# Revit family: TSM Betonschraube Ansatzschraube TSM 6, vz M 8x 16
name_source: partatom
category: Allgemeines Modell
revit_build: Autodesk Revit 2017 (Build: 20190507_1515(x64)
units: mm (PartAtom-declared; Revit-internal decimal feet)

## family parameters
Arbeitsebenenbasiert = Ja
Beim Laden mit Abzugskörper schneiden = Nein
Bemaßung runder Anschluss = Durchmesser verwenden
Gemeinsam genutzt = Ja
Immer vertikal = Nein
Kann Basisbauteil für Bewehrung sein = Nein
Raumberechnungspunkt = Nein
Teiletyp = Normal

## types (1)
- TSM Betonschraube Ansatzschraube TSM 6, vz M 8x 16
    Artikelnummer = 2230002
    Außengewinde = M8 x 16
    Bohrerdurchmesser = 6 mm
    EAN = 4260116911737
    Fabrikat = Toge
    Firma = MEFA Befestigungs- und Montagesysteme GmbH
    Form Kopf = Ansatzschraube
    Gewicht = 0.02 kg
    Gewicht pro Bauteil = 0.02 kg
    Kurztext1 = Betonschraube TSM 6
    Kurztext2 = L= 55 mm Ansatzschraube M8 x 16
    Länge = 55 mm  [stored 0.180446 ft]
    Material = Stahl
    Mengeneinheit = St
    Oberflaeche = Zinklamellenbeschichtet
    Vorgabe-Ansicht = 1219 mm
    max. Klemmstärke = 0 mm  [stored 0 ft]
    min. Bohrlochtiefe = 65 mm
    vpe = 100 St

note: [stored X ft] marks values corroborated as IEEE doubles in the binary element streams (Revit-internal decimal feet)
